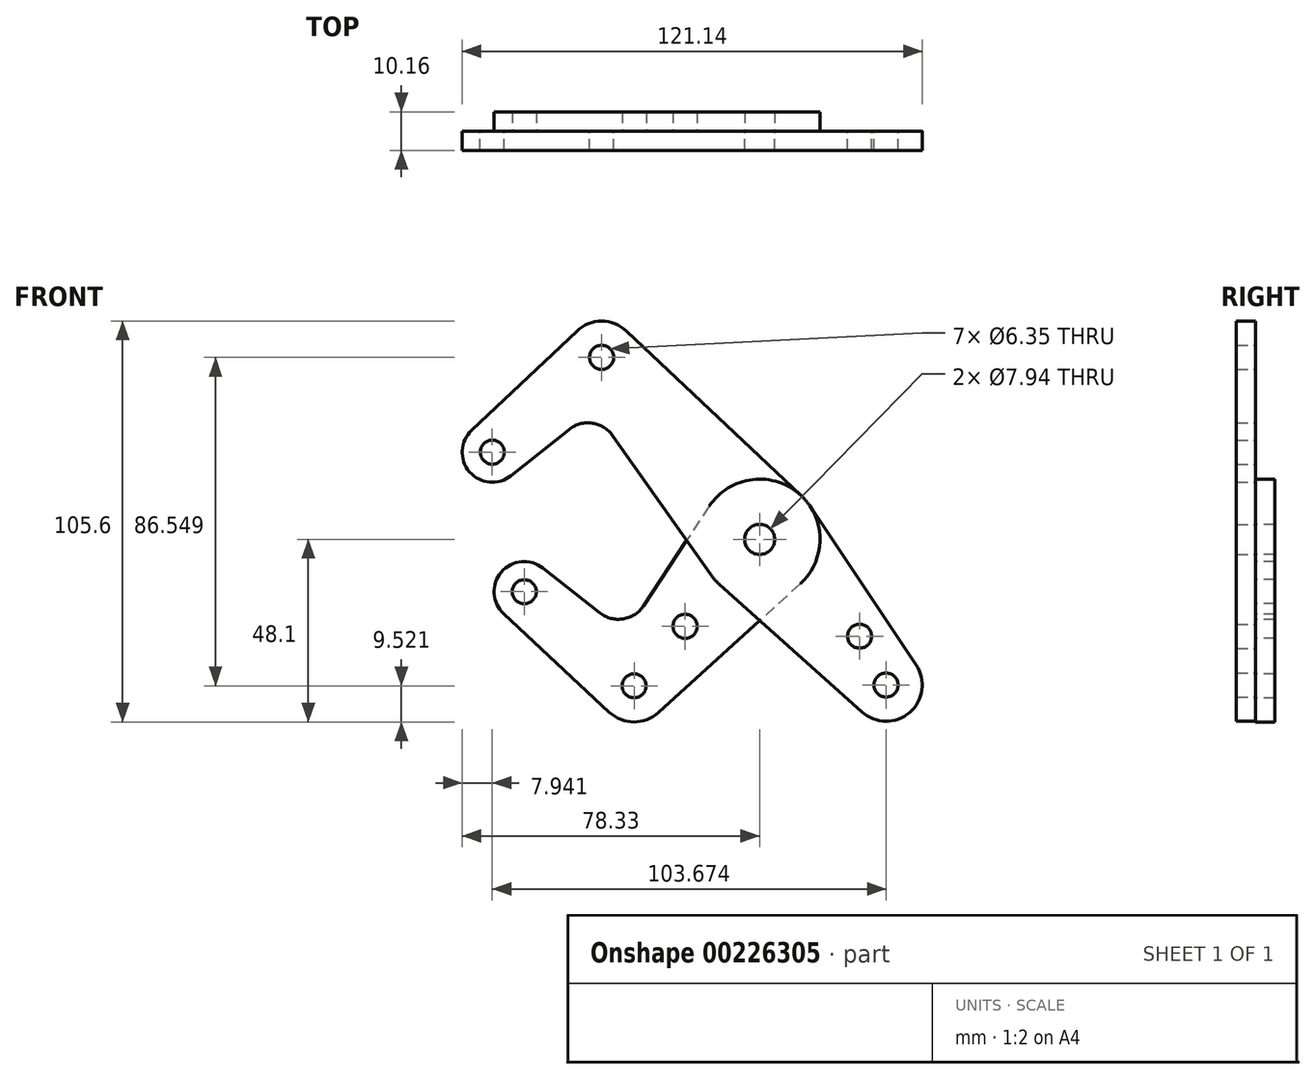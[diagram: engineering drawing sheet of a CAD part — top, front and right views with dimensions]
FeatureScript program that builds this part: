
annotation { "Feature Type Name" : "Feature", "Feature Type Description" : "" }
export const myFeature = defineFeature(function(context is Context, id is Id, definition is map)
    precondition{}
    {
        {
            var Q0;
            Q0=qCreatedBy(makeId("Front.planeOp"),FACE);
            var sketch = newSketch(context, id + "F0", { "sketchPlane" : qUnion([Q0])});
            skLineSegment(sketch, "E0", {"start": v(-41.6, 47.97) * mm, "end": v(41.6, -47.97) * mm, "construction": true});
            skCircle(sketch, "E1", {"center": v(0, 0) * mm, "radius": 3.18 * mm});
            skCircle(sketch, "E2", {"center": v(33.29, -38.38) * mm, "radius": 3.18 * mm});
            skCircle(sketch, "E3", {"center": v(-41.6, 47.97) * mm, "radius": 3.18 * mm});
            skCircle(sketch, "E4", {"center": v(-70.39, 23) * mm, "radius": 3.18 * mm});
            skLineSegment(sketch, "E5", {"start": v(-41.6, 47.97) * mm, "end": v(-70.39, 23) * mm, "construction": true});
            skCircle(sketch, "E6", {"center": v(33.29, -38.38) * mm, "radius": 9.53 * mm});
            skCircle(sketch, "E7", {"center": v(-70.39, 23) * mm, "radius": 7.94 * mm});
            skCircle(sketch, "E8", {"center": v(-41.6, 47.97) * mm, "radius": 9.53 * mm});
            skLineSegment(sketch, "E9", {"start": v(-75.83, 28.78) * mm, "end": v(-48.14, 54.9) * mm});
            skLineSegment(sketch, "E10", {"start": v(-65.44, 16.8) * mm, "end": v(-50.15, 28.98) * mm});
            skCircle(sketch, "E11", {"center": v(0, 0) * mm, "radius": 15.88 * mm});
            skLineSegment(sketch, "E12", {"start": v(-35.07, 54.9) * mm, "end": v(10.9, 11.55) * mm});
            skLineSegment(sketch, "E13", {"start": v(-38.72, 27.35) * mm, "end": v(-12.97, -9.15) * mm});
            skLineSegment(sketch, "E14", {"start": v(-10.6, -11.82) * mm, "end": v(26.93, -45.47) * mm});
            skLineSegment(sketch, "E15", {"start": v(13.2, 8.82) * mm, "end": v(41.2, -33.08) * mm});
            skArc(sketch, "E16.filletArc", {"start": v(-38.72, 27.35) * mm, "mid": v(-44.08, 30.63) * mm, "end": v(-50.15, 28.98) * mm});
            skLineSegment(sketch, "E17", {"start": v(0, 0) * mm, "end": v(-33.05, -38.58) * mm, "construction": true});
            skLineSegment(sketch, "E18", {"start": v(-33.05, -38.58) * mm, "end": v(-61.98, -13.8) * mm, "construction": true});
            skCircle(sketch, "E19", {"center": v(-61.98, -13.8) * mm, "radius": 3.18 * mm});
            skCircle(sketch, "E20", {"center": v(-33.05, -38.58) * mm, "radius": 3.18 * mm});
            skCircle(sketch, "E21", {"center": v(-61.98, -13.8) * mm, "radius": 7.94 * mm});
            skCircle(sketch, "E22", {"center": v(-33.05, -38.58) * mm, "radius": 9.53 * mm});
            skLineSegment(sketch, "E23", {"start": v(-57.08, -7.55) * mm, "end": v(-42.08, -19.35) * mm});
            skLineSegment(sketch, "E24", {"start": v(-67.4, -19.6) * mm, "end": v(-39.54, -45.55) * mm});
            skLineSegment(sketch, "E25", {"start": v(-13.25, 8.74) * mm, "end": v(-30.55, -17.48) * mm});
            skLineSegment(sketch, "E26", {"start": v(10.67, -11.75) * mm, "end": v(-26.65, -45.63) * mm});
            skArc(sketch, "E27.filletArc", {"start": v(-42.08, -19.35) * mm, "mid": v(-35.9, -20.95) * mm, "end": v(-30.55, -17.48) * mm});
            skCircle(sketch, "E28", {"center": v(-19.62, -22.9) * mm, "radius": 3.18 * mm});
            skCircle(sketch, "E29", {"center": v(26.32, -25.5) * mm, "radius": 3.18 * mm});
            skLineSegment(sketch, "E30", {"start": v(26.32, -25.5) * mm, "end": v(23.92, -27.58) * mm, "construction": true});
            skCircle(sketch, "E31", {"center": v(0, 0) * mm, "radius": 3.97 * mm});
            skSolve(sketch);
        }
        {
            var Q0;
            {var subQ1=sQuery(id+"F0.wireOp",EDGE,"E9");Q0=makeQuery(id+"F0.imprint","IMPRINT",FACE,{"disambiguationData":[TD([[makeQuery(id+"F0.imprint","IMPRINT",EDGE,{"derivedFrom":subQ1}),-1.0]])]});}
            var Q1;
            Q1=makeQuery(id+"F0.imprint","IMPRINT",FACE,{"disambiguationData":[TD([[makeQuery(id+"F0.imprint","IMPRINT",EDGE,{"derivedFrom":sQuery(id+"F0.wireOp",EDGE,"E31")}),-1.0]])]});
            var Q2;
            {var subQ0=sQuery(id+"F0.wireOp",EDGE,"E13");var subQ1=sQuery(id+"F0.wireOp",EDGE,"E11");var subQ2=makeQuery(id+"F0.imprint","INTERSECT",VERTEX,{"derivedFrom":[subQ1,subQ0]});Q2=makeQuery(id+"F0.imprint","IMPRINT",FACE,{"disambiguationData":[TD([[makeQuery(id+"F0.imprint","IMPRINT",EDGE,{"disambiguationData":[TD([[subQ2,1.0]])],"derivedFrom":subQ1}),-1.0]])]});}
            var Q3;
            {var subQ0=sQuery(id+"F0.wireOp",EDGE,"E14");var subQ1=sQuery(id+"F0.wireOp",EDGE,"E11");var subQ2=makeQuery(id+"F0.imprint","INTERSECT",VERTEX,{"derivedFrom":[subQ1,subQ0]});Q3=makeQuery(id+"F0.imprint","IMPRINT",FACE,{"disambiguationData":[TD([[makeQuery(id+"F0.imprint","IMPRINT",EDGE,{"disambiguationData":[TD([[subQ2,-1.0]])],"derivedFrom":subQ1}),-1.0]])]});}
            var Q4;
            {var subQ0=sQuery(id+"F0.wireOp",EDGE,"E15");Q4=makeQuery(id+"F0.imprint","IMPRINT",FACE,{"disambiguationData":[TD([[makeQuery(id+"F0.imprint","IMPRINT",EDGE,{"derivedFrom":subQ0}),-1.0]])]});}
            var Q5;
            Q5=makeQuery(id+"F0.imprint","IMPRINT",FACE,{"disambiguationData":[TD([[makeQuery(id+"F0.imprint","IMPRINT",EDGE,{"derivedFrom":sQuery(id+"F0.wireOp",EDGE,"E2")}),-1.0]])]});
            var Q6;
            Q6=makeQuery(id+"F0.imprint","IMPRINT",FACE,{"disambiguationData":[TD([[makeQuery(id+"F0.imprint","IMPRINT",EDGE,{"derivedFrom":sQuery(id+"F0.wireOp",EDGE,"E4")}),-1.0]])]});
            var Q7;
            Q7=makeQuery(id+"F0.imprint","IMPRINT",FACE,{"disambiguationData":[TD([[makeQuery(id+"F0.imprint","IMPRINT",EDGE,{"derivedFrom":sQuery(id+"F0.wireOp",EDGE,"E3")}),-1.0]])]});
            extrude(context, id + "F1", {"entities" : qUnion([Q0, Q1, Q2, Q3, Q4, Q5, Q6, Q7]), "depth" : 5.08 * mm});
        }
        {
            var Q0;
            {var subQ10=sQuery(id+"F0.wireOp",EDGE,"E23");Q0=makeQuery(id+"F0.imprint","IMPRINT",FACE,{"disambiguationData":[TD([[makeQuery(id+"F0.imprint","IMPRINT",EDGE,{"derivedFrom":subQ10}),-1.0]])]});}
            var Q1;
            Q1=makeQuery(id+"F0.imprint","IMPRINT",FACE,{"disambiguationData":[TD([[makeQuery(id+"F0.imprint","IMPRINT",EDGE,{"derivedFrom":sQuery(id+"F0.wireOp",EDGE,"E31")}),-1.0]])]});
            var Q2;
            Q2=makeQuery(id+"F0.imprint","IMPRINT",FACE,{"disambiguationData":[TD([[makeQuery(id+"F0.imprint","IMPRINT",EDGE,{"derivedFrom":sQuery(id+"F0.wireOp",EDGE,"E20")}),-1.0]])]});
            var Q3;
            Q3=makeQuery(id+"F0.imprint","IMPRINT",FACE,{"disambiguationData":[TD([[makeQuery(id+"F0.imprint","IMPRINT",EDGE,{"derivedFrom":sQuery(id+"F0.wireOp",EDGE,"E19")}),-1.0]])]});
            var Q4;
            {var subQ0=sQuery(id+"F0.wireOp",EDGE,"E14");var subQ1=sQuery(id+"F0.wireOp",EDGE,"E11");var subQ2=makeQuery(id+"F0.imprint","INTERSECT",VERTEX,{"derivedFrom":[subQ1,subQ0]});Q4=makeQuery(id+"F0.imprint","IMPRINT",FACE,{"disambiguationData":[TD([[makeQuery(id+"F0.imprint","IMPRINT",EDGE,{"disambiguationData":[TD([[subQ2,-1.0]])],"derivedFrom":subQ1}),-1.0]])]});}
            var Q5;
            {var subQ0=sQuery(id+"F0.wireOp",EDGE,"E13");var subQ1=sQuery(id+"F0.wireOp",EDGE,"E11");var subQ2=makeQuery(id+"F0.imprint","INTERSECT",VERTEX,{"derivedFrom":[subQ1,subQ0]});Q5=makeQuery(id+"F0.imprint","IMPRINT",FACE,{"disambiguationData":[TD([[makeQuery(id+"F0.imprint","IMPRINT",EDGE,{"disambiguationData":[TD([[subQ2,1.0]])],"derivedFrom":subQ1}),-1.0]])]});}
            extrude(context, id + "F2", {"entities" : qUnion([Q0, Q1, Q2, Q3, Q4, Q5]), "oppositeDirection" : true, "depth" : 5.08 * mm});
        }
    });
